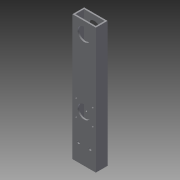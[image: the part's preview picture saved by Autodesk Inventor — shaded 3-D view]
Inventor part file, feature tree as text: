
AUTODESK INVENTOR PART (.ipt)
format: ipt  version: 2013 (Build 170138000, 138)  size: 129,024 bytes
history: native  units: in
note: dims shown in document units (in); Inventor stores cm internally (conversion verified against a paired STEP export)
features: extrude x4, sketch x4
ambient origin geometry x8: Origin, YZ Plane, XZ Plane, XY Plane, X Axis, Y Axis, Z Axis, Center Point
bodies: Solid1 (feature_tree)
feature tree (8):
  extrude  "Extrusion1"  Depth=1.0in
  extrude  "Extrusion2"  Depth=0.75in
  extrude  "Extrusion3"  Depth=1.5in
  extrude  "Extrusion4"  Depth=0.5in
  sketch  "Sketch1"  dims[d0=2.0in d1=1.0in]
  sketch  "Sketch2"  dims[d2=1.75in d3=0.75in]
  sketch  "Sketch3"  dims[d4=10.75in d5=0.0in d6=1.5in]
  sketch  "Sketch4"  dims[d7=90.0deg d8=0.5in d9=90.0deg d10=1.0in d11=0.0in d12=0.25in d13=0.25in d14=8.0in d15=0.0in d16=1.0in d17=90.0deg d18=1.125in d19=1.0in d20=0.0in d21=2.0in d22=3.0in d23=2.0in d24=2.0in d25=1.125in d29=0.16in d30=0.16in d31=0.16in d32=0.16in d33=1.0in d34=0.0in]
